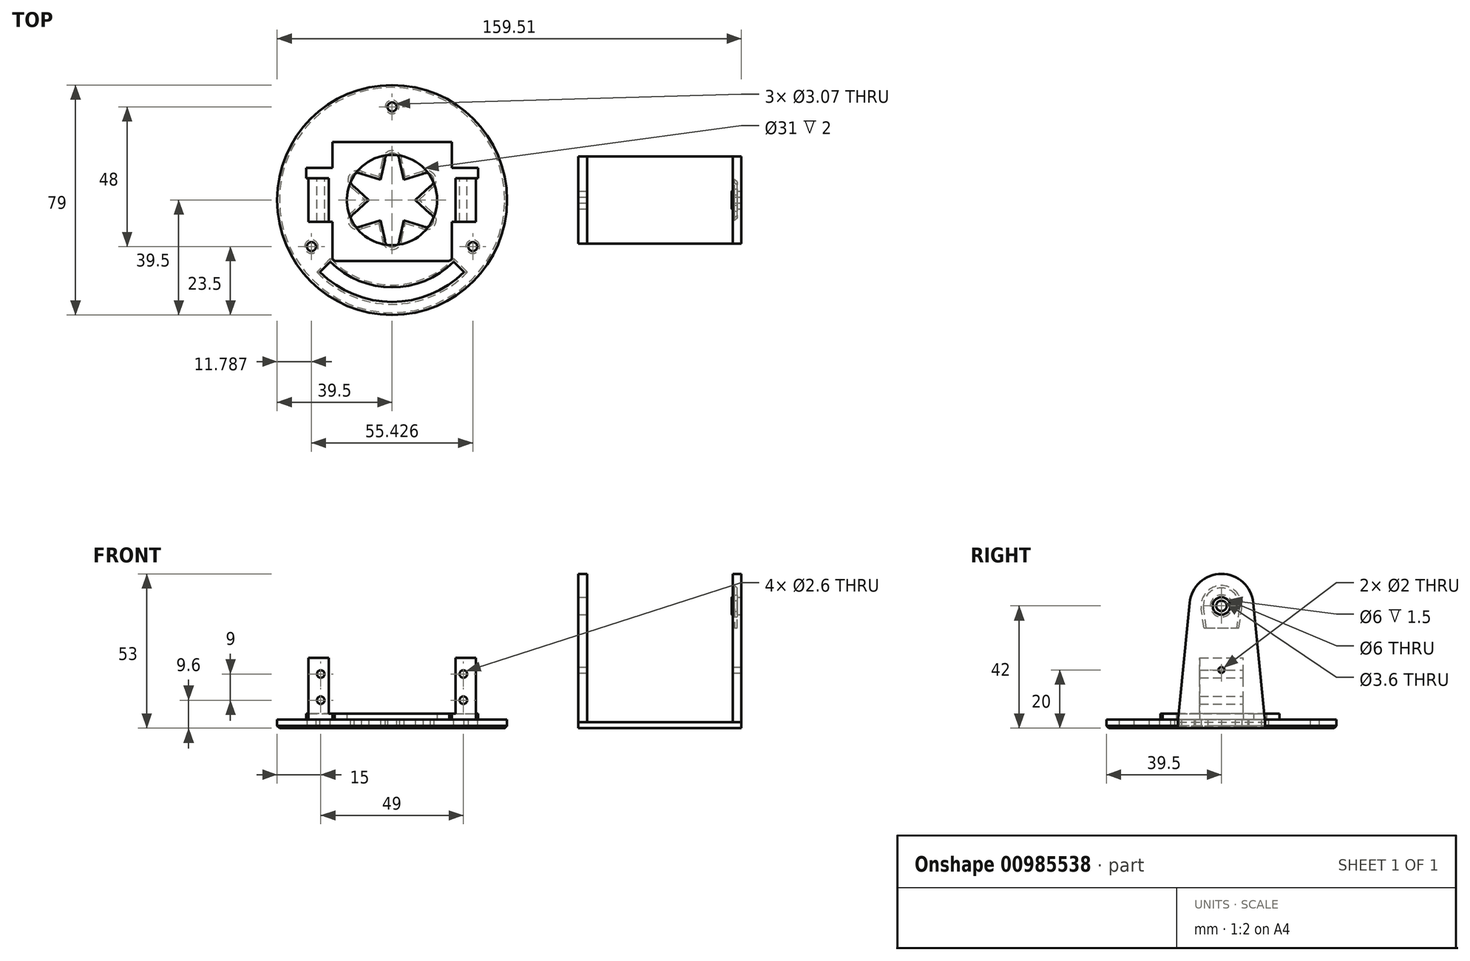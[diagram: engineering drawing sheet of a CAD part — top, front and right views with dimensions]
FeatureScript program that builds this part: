
annotation { "Feature Type Name" : "Feature", "Feature Type Description" : "" }
export const myFeature = defineFeature(function(context is Context, id is Id, definition is map)
    precondition{}
    {
        {
            var Q0;
            Q0=qCreatedBy(makeId("Top.planeOp"),FACE);
            var sketch = newSketch(context, id + "F0", { "sketchPlane" : qUnion([Q0])});
            skCircle(sketch, "E0", {"center": v(0, 0) * mm, "radius": 39.5 * mm});
            skLineSegment(sketch, "E1", {"start": v(0, 6.93) * mm, "end": v(0, 13.68) * mm});
            skArc(sketch, "E2", {"start": v(2.5, 13.68) * mm, "mid": v(0, 16.18) * mm, "end": v(-2.5, 13.68) * mm});
            skLineSegment(sketch, "E3", {"start": v(2.5, 13.68) * mm, "end": v(4, 6.93) * mm});
            skLineSegment(sketch, "E4", {"start": v(-2.5, 13.68) * mm, "end": v(-4, 6.93) * mm});
            skLineSegment(sketch, "E5", {"start": v(0, 0) * mm, "end": v(0, 6.93) * mm});
            skLineSegment(sketch, "E6", {"start": v(-4, 6.93) * mm, "end": v(0, 0) * mm});
            skLineSegment(sketch, "E7", {"start": v(4, 6.93) * mm, "end": v(0, 0) * mm});
            skLineSegment(sketch, "E8.1.0", {"start": v(-10.6, 9) * mm, "end": v(-4, 6.93) * mm});
            skLineSegment(sketch, "E8.1.1", {"start": v(-8, 0) * mm, "end": v(0, 0) * mm});
            skLineSegment(sketch, "E8.1.2", {"start": v(-6, 3.46) * mm, "end": v(-11.85, 6.84) * mm});
            skLineSegment(sketch, "E8.1.3", {"start": v(0, 0) * mm, "end": v(-6, 3.46) * mm});
            skArc(sketch, "E8.1.4", {"start": v(-10.6, 9) * mm, "mid": v(-14.01, 8.09) * mm, "end": v(-13.1, 4.67) * mm});
            skLineSegment(sketch, "E8.1.5", {"start": v(-13.1, 4.67) * mm, "end": v(-8, 0) * mm});
            skLineSegment(sketch, "E8.2.0", {"start": v(-13.1, -4.67) * mm, "end": v(-8, 0) * mm});
            skLineSegment(sketch, "E8.2.1", {"start": v(-4, -6.93) * mm, "end": v(0, 0) * mm});
            skLineSegment(sketch, "E8.2.2", {"start": v(-6, -3.46) * mm, "end": v(-11.85, -6.84) * mm});
            skLineSegment(sketch, "E8.2.3", {"start": v(0, 0) * mm, "end": v(-6, -3.46) * mm});
            skArc(sketch, "E8.2.4", {"start": v(-13.1, -4.67) * mm, "mid": v(-14.01, -8.09) * mm, "end": v(-10.6, -9) * mm});
            skLineSegment(sketch, "E8.2.5", {"start": v(-10.6, -9) * mm, "end": v(-4, -6.93) * mm});
            skLineSegment(sketch, "E8.2.6", {"start": v(-8, 0) * mm, "end": v(0, 0) * mm});
            skLineSegment(sketch, "E8.3.0", {"start": v(-2.5, -13.68) * mm, "end": v(-4, -6.93) * mm});
            skLineSegment(sketch, "E8.3.1", {"start": v(4, -6.93) * mm, "end": v(0, 0) * mm});
            skLineSegment(sketch, "E8.3.2", {"start": v(0, -6.93) * mm, "end": v(0, -13.68) * mm});
            skLineSegment(sketch, "E8.3.3", {"start": v(0, 0) * mm, "end": v(0, -6.93) * mm});
            skArc(sketch, "E8.3.4", {"start": v(-2.5, -13.68) * mm, "mid": v(0, -16.18) * mm, "end": v(2.5, -13.68) * mm});
            skLineSegment(sketch, "E8.3.5", {"start": v(2.5, -13.68) * mm, "end": v(4, -6.93) * mm});
            skLineSegment(sketch, "E8.3.6", {"start": v(-4, -6.93) * mm, "end": v(0, 0) * mm});
            skLineSegment(sketch, "E8.4.0", {"start": v(10.6, -9) * mm, "end": v(4, -6.93) * mm});
            skLineSegment(sketch, "E8.4.1", {"start": v(8, 0) * mm, "end": v(0, 0) * mm});
            skLineSegment(sketch, "E8.4.2", {"start": v(6, -3.46) * mm, "end": v(11.85, -6.84) * mm});
            skLineSegment(sketch, "E8.4.3", {"start": v(0, 0) * mm, "end": v(6, -3.46) * mm});
            skArc(sketch, "E8.4.4", {"start": v(10.6, -9) * mm, "mid": v(14.01, -8.09) * mm, "end": v(13.1, -4.67) * mm});
            skLineSegment(sketch, "E8.4.5", {"start": v(13.1, -4.67) * mm, "end": v(8, 0) * mm});
            skLineSegment(sketch, "E8.4.6", {"start": v(4, -6.93) * mm, "end": v(0, 0) * mm});
            skLineSegment(sketch, "E8.5.0", {"start": v(13.1, 4.67) * mm, "end": v(8, 0) * mm});
            skLineSegment(sketch, "E8.5.2", {"start": v(6, 3.46) * mm, "end": v(11.85, 6.84) * mm});
            skLineSegment(sketch, "E8.5.3", {"start": v(0, 0) * mm, "end": v(6, 3.46) * mm});
            skArc(sketch, "E8.5.4", {"start": v(13.1, 4.67) * mm, "mid": v(14.01, 8.09) * mm, "end": v(10.6, 9) * mm});
            skLineSegment(sketch, "E8.5.5", {"start": v(10.6, 9) * mm, "end": v(4, 6.93) * mm});
            skLineSegment(sketch, "E8.5.6", {"start": v(8, 0) * mm, "end": v(0, 0) * mm});
            skCircle(sketch, "E9", {"center": v(0, 32) * mm, "radius": 1.53 * mm});
            skCircle(sketch, "E10.1.0", {"center": v(-27.71, -16) * mm, "radius": 1.53 * mm});
            skCircle(sketch, "E10.2.0", {"center": v(27.71, -16) * mm, "radius": 1.53 * mm});
            skSolve(sketch);
        }
        {
            var Q0;
            Q0=qSketchRegion(id+"F0",true);
            extrude(context, id + "F1", {"entities" : qUnion([Q0]), "depth" : 3 * mm, "offsetDistance" : 25 * mm});
        }
        {
            var Q0;
            Q0=makeQuery(id+"F1.opExtrude","CAP_FACE",FACE,{"disambiguationData":[OSD([sQuery(id+"F0.wireOp",EDGE,"E0"),sQuery(id+"F0.wireOp",EDGE,"tsmetPdh-uBPC-VMs7-KmTe-eYArdxmcJazE.bottom"),sQuery(id+"F0.wireOp",EDGE,"tsmetPdh-uBPC-VMs7-KmTe-eYArdxmcJazE.top"),sQuery(id+"F0.wireOp",EDGE,"tsmetPdh-uBPC-VMs7-KmTe-eYArdxmcJazE.left"),sQuery(id+"F0.wireOp",EDGE,"tsmetPdh-uBPC-VMs7-KmTe-eYArdxmcJazE.right"),sQuery(id+"F0.wireOp",EDGE,"4L8ITVok-LRZH-0QI6-TBfI-3UofOHPGhmV9.bottom"),sQuery(id+"F0.wireOp",EDGE,"4L8ITVok-LRZH-0QI6-TBfI-3UofOHPGhmV9.top"),sQuery(id+"F0.wireOp",EDGE,"4L8ITVok-LRZH-0QI6-TBfI-3UofOHPGhmV9.right"),sQuery(id+"F0.wireOp",EDGE,"eeb0b982-9b75-4dce-bc6a-ac392abf8ab80.MirrorCS"),sQuery(id+"F0.wireOp",EDGE,"f73e68d2-0441-471e-96cc-38fd0b7eeaf80.MirrorCS"),sQuery(id+"F0.wireOp",EDGE,"16b79043-1bf6-4525-a8b7-725060b6b32b0.MirrorCS"),sQuery(id+"F0.wireOp",EDGE,"p6ZJKreq-HdhA-XT4y-qAaR-6FUMRbpX3NII"),sQuery(id+"F0.wireOp",EDGE,"b497d003-922a-44de-87ad-1ec905d6c705.1.0"),sQuery(id+"F0.wireOp",EDGE,"b497d003-922a-44de-87ad-1ec905d6c705.2.0"),sQuery(id+"F0.wireOp",EDGE,"b497d003-922a-44de-87ad-1ec905d6c705.3.0"),sQuery(id+"F0.wireOp",EDGE,"b497d003-922a-44de-87ad-1ec905d6c705.4.0"),sQuery(id+"F0.wireOp",EDGE,"b497d003-922a-44de-87ad-1ec905d6c705.5.0")])],"isStart":false});
            var sketch = newSketch(context, id + "F2", { "sketchPlane" : qUnion([Q0])});
            skLineSegment(sketch, "E11.bottom", {"start": v(20.5, -21) * mm, "end": v(-20.5, -21) * mm});
            skLineSegment(sketch, "E11.top", {"start": v(20.5, 20) * mm, "end": v(-20.5, 20) * mm});
            skLineSegment(sketch, "E11.left", {"start": v(20.5, -21) * mm, "end": v(20.5, 20) * mm});
            skLineSegment(sketch, "E11.right", {"start": v(-20.5, -21) * mm, "end": v(-20.5, 20) * mm});
            skPoint(sketch, "E11.middle", {"position": v(0, -0.5) * mm});
            skPoint(sketch, "E12", {"position": v(0, -3.9) * mm});
            skLineSegment(sketch, "E13.bottom", {"start": v(20.5, 11) * mm, "end": v(29.5, 11) * mm});
            skLineSegment(sketch, "E13.top", {"start": v(20.5, 7.5) * mm, "end": v(29.5, 7.5) * mm});
            skLineSegment(sketch, "E13.left", {"start": v(20.5, 11) * mm, "end": v(20.5, 7.5) * mm});
            skLineSegment(sketch, "E13.right", {"start": v(29.5, 11) * mm, "end": v(29.5, 7.5) * mm});
            skPoint(sketch, "E14.center", {"position": v(0, 0) * mm});
            skLineSegment(sketch, "E15", {"start": v(28.75, 7.5) * mm, "end": v(28.75, -7.5) * mm});
            skLineSegment(sketch, "E16", {"start": v(28.75, -7.5) * mm, "end": v(19.95, -7.5) * mm});
            skLineSegment(sketch, "E17.MirrorCS", {"start": v(-20.5, 11) * mm, "end": v(-29.5, 11) * mm});
            skLineSegment(sketch, "E18.MirrorCS", {"start": v(-29.5, 11) * mm, "end": v(-29.5, 7.5) * mm});
            skLineSegment(sketch, "E19.MirrorCS", {"start": v(-20.5, 7.5) * mm, "end": v(-29.5, 7.5) * mm});
            skLineSegment(sketch, "E20.MirrorCS", {"start": v(-28.75, 7.5) * mm, "end": v(-28.75, -7.5) * mm});
            skLineSegment(sketch, "E21.MirrorCS", {"start": v(-28.75, -7.5) * mm, "end": v(-19.95, -7.5) * mm});
            skCircle(sketch, "E22", {"center": v(0, 0) * mm, "radius": 15.5 * mm});
            skSolve(sketch);
        }
        {
            var Q0;
            {var subQ6=sQuery(id+"F2.wireOp",EDGE,"E15");var subQ9=sQuery(id+"F2.wireOp",EDGE,"E17.MirrorCS");var subQ15=sQuery(id+"F2.wireOp",EDGE,"E22");var subQ16=makeQuery(id+"F1.opExtrude","CAP_EDGE",EDGE,{"disambiguationData":[OSD([sQuery(id+"F0.wireOp",EDGE,"E8.1.4")])],"isStart":false});var subQ17=makeQuery(id+"F2.imprint","INTERSECT",VERTEX,{"disambiguationData":[OD(0.0)],"derivedFrom":[subQ16,subQ15]});var subQ21=makeQuery(id+"F1.opExtrude","CAP_EDGE",EDGE,{"disambiguationData":[OSD([sQuery(id+"F0.wireOp",EDGE,"E8.3.4")])],"isStart":false});var subQ23=makeQuery(id+"F1.opExtrude","CAP_EDGE",EDGE,{"disambiguationData":[OSD([sQuery(id+"F0.wireOp",EDGE,"E8.4.4")])],"isStart":false});var subQ24=makeQuery(id+"F2.imprint","INTERSECT",VERTEX,{"disambiguationData":[OD(0.0)],"derivedFrom":[subQ23,subQ15]});var subQ25=sQuery(id+"F2.wireOp",EDGE,"E11.bottom");var subQ29=makeQuery(id+"F1.opExtrude","CAP_EDGE",EDGE,{"disambiguationData":[OSD([sQuery(id+"F0.wireOp",EDGE,"E8.2.4")])],"isStart":false});var subQ31=makeQuery(id+"F2.imprint","INTERSECT",VERTEX,{"disambiguationData":[OD(0.0)],"derivedFrom":[subQ21,subQ15]});var subQ32=makeQuery(id+"F1.opExtrude","CAP_EDGE",EDGE,{"disambiguationData":[OSD([sQuery(id+"F0.wireOp",EDGE,"E2")])],"isStart":false});var subQ33=makeQuery(id+"F2.imprint","INTERSECT",VERTEX,{"disambiguationData":[OD(0.0)],"derivedFrom":[subQ32,subQ15]});var subQ36=sQuery(id+"F2.wireOp",EDGE,"E13.bottom");var subQ39=makeQuery(id+"F2.imprint","INTERSECT",VERTEX,{"disambiguationData":[OD(0.0)],"derivedFrom":[subQ29,subQ15]});var subQ40=makeQuery(id+"F1.opExtrude","CAP_EDGE",EDGE,{"disambiguationData":[OSD([sQuery(id+"F0.wireOp",EDGE,"E8.5.4")])],"isStart":false});var subQ41=makeQuery(id+"F2.imprint","INTERSECT",VERTEX,{"disambiguationData":[OD(0.0)],"derivedFrom":[subQ40,subQ15]});var subQ48=sQuery(id+"F2.wireOp",EDGE,"E20.MirrorCS");Q0=qUnion([makeQuery(id+"F2.imprint","IMPRINT",FACE,{"disambiguationData":[TD([[makeQuery(id+"F2.imprint","IMPRINT",EDGE,{"derivedFrom":subQ9}),1.0]])]}),makeQuery(id+"F2.imprint","IMPRINT",FACE,{"disambiguationData":[TD([[makeQuery(id+"F2.imprint","IMPRINT",EDGE,{"disambiguationData":[TD([[subQ17,-1.0]])],"derivedFrom":subQ15}),-1.0]])]}),makeQuery(id+"F2.imprint","IMPRINT",FACE,{"disambiguationData":[TD([[makeQuery(id+"F2.imprint","IMPRINT",EDGE,{"derivedFrom":subQ36}),-1.0]])]}),makeQuery(id+"F2.imprint","IMPRINT",FACE,{"disambiguationData":[TD([[makeQuery(id+"F2.imprint","IMPRINT",EDGE,{"disambiguationData":[TD([[subQ24,-1.0]])],"derivedFrom":subQ15}),-1.0]])]}),makeQuery(id+"F2.imprint","IMPRINT",FACE,{"disambiguationData":[TD([[makeQuery(id+"F2.imprint","IMPRINT",EDGE,{"disambiguationData":[TD([[subQ39,-1.0]])],"derivedFrom":subQ15}),-1.0]])]}),makeQuery(id+"F2.imprint","IMPRINT",FACE,{"disambiguationData":[TD([[makeQuery(id+"F2.imprint","IMPRINT",EDGE,{"derivedFrom":subQ48}),1.0]])]}),makeQuery(id+"F2.imprint","IMPRINT",FACE,{"disambiguationData":[TD([[makeQuery(id+"F2.imprint","IMPRINT",EDGE,{"disambiguationData":[TD([[subQ41,1.0]])],"derivedFrom":subQ15}),-1.0]])]}),makeQuery(id+"F2.imprint","IMPRINT",FACE,{"disambiguationData":[TD([[makeQuery(id+"F2.imprint","IMPRINT",EDGE,{"disambiguationData":[TD([[subQ31,-1.0]])],"derivedFrom":subQ15}),-1.0]])]}),makeQuery(id+"F2.imprint","IMPRINT",FACE,{"disambiguationData":[TD([[makeQuery(id+"F2.imprint","IMPRINT",EDGE,{"disambiguationData":[TD([[subQ33,-1.0]])],"derivedFrom":subQ15}),-1.0]])]}),makeQuery(id+"F2.imprint","IMPRINT",FACE,{"disambiguationData":[TD([[makeQuery(id+"F2.imprint","IMPRINT",EDGE,{"derivedFrom":subQ25}),-1.0]])]}),makeQuery(id+"F2.imprint","IMPRINT",FACE,{"disambiguationData":[TD([[makeQuery(id+"F2.imprint","IMPRINT",EDGE,{"derivedFrom":subQ6}),-1.0]])]})]);}
            extrude(context, id + "F3", {"entities" : qUnion([Q0]), "operationType" : NewBodyOperationType.ADD, "depth" : 2 * mm, "offsetDistance" : 25 * mm});
        }
        {
            var Q0;
            Q0=qCreatedBy(makeId("Front.planeOp"),FACE);
            var sketch = newSketch(context, id + "F4", { "sketchPlane" : qUnion([Q0])});
            skLineSegment(sketch, "E23", {"start": v(9.75, 14.1) * mm, "end": v(14.35, 14.1) * mm});
            skCircle(sketch, "E24", {"center": v(24.5, 18.6) * mm, "radius": 1.3 * mm});
            skLineSegment(sketch, "E25.bottom", {"start": v(21.75, 4) * mm, "end": v(21.75, 24.2) * mm});
            skLineSegment(sketch, "E25.top", {"start": v(28.75, 4) * mm, "end": v(28.75, 24.2) * mm});
            skLineSegment(sketch, "E25.left", {"start": v(21.75, 4) * mm, "end": v(28.75, 4) * mm});
            skLineSegment(sketch, "E25.right", {"start": v(21.75, 24.2) * mm, "end": v(28.75, 24.2) * mm});
            skPoint(sketch, "E25.middle", {"position": v(25.25, 14.1) * mm});
            skCircle(sketch, "E26.MirrorC", {"center": v(24.5, 9.6) * mm, "radius": 1.3 * mm});
            skLineSegment(sketch, "E27", {"start": v(0, 7.04) * mm, "end": v(0, 23.64) * mm});
            skPoint(sketch, "E28.MirrorP", {"position": v(-25.25, 14.1) * mm});
            skLineSegment(sketch, "E29.MirrorCS", {"start": v(-21.75, 24.2) * mm, "end": v(-28.75, 24.2) * mm});
            skLineSegment(sketch, "E30.MirrorCS", {"start": v(-28.75, 4) * mm, "end": v(-28.75, 24.2) * mm});
            skLineSegment(sketch, "E31.MirrorCS", {"start": v(-21.75, 4) * mm, "end": v(-21.75, 24.2) * mm});
            skCircle(sketch, "E32.MirrorC", {"center": v(-24.5, 9.6) * mm, "radius": 1.3 * mm});
            skLineSegment(sketch, "E33.MirrorCS", {"start": v(-21.75, 4) * mm, "end": v(-28.75, 4) * mm});
            skCircle(sketch, "E34.MirrorC", {"center": v(-24.5, 18.6) * mm, "radius": 1.3 * mm});
            skSolve(sketch);
        }
        {
            var Q0;
            Q0 = qSketchRegion(id + "F4", true);
            extrude(context, id + "F5", {"entities" : qUnion([Q0]), "operationType" : NewBodyOperationType.ADD, "endBound" : BoundingType.SYMMETRIC, "depth" : 15 * mm, "offsetDistance" : 25 * mm});
        }
        {
            var Q0;
            Q0=qCreatedBy(makeId("Top.planeOp"),FACE);
            var sketch = newSketch(context, id + "F6", { "sketchPlane" : qUnion([Q0])});
            skLineSegment(sketch, "E35.bottom", {"start": v(120.01, -15) * mm, "end": v(64.01, -15) * mm});
            skLineSegment(sketch, "E35.top", {"start": v(120.01, 15) * mm, "end": v(64.01, 15) * mm});
            skLineSegment(sketch, "E35.left", {"start": v(120.01, -15) * mm, "end": v(120.01, 15) * mm});
            skLineSegment(sketch, "E35.right", {"start": v(64.01, -15) * mm, "end": v(64.01, 15) * mm});
            skPoint(sketch, "E35.middle", {"position": v(92.01, 0) * mm});
            skSolve(sketch);
        }
        {
            var Q0;
            Q0=makeQuery(id+"F6.imprint","IMPRINT",FACE,{"disambiguationData":[TD([[makeQuery(id+"F6.imprint","IMPRINT",EDGE,{"derivedFrom":sQuery(id+"F6.wireOp",EDGE,"E35.bottom")}),-1.0]])]});
            extrude(context, id + "F7", {"entities" : qUnion([Q0]), "depth" : 2 * mm, "offsetDistance" : 25 * mm});
        }
        {
            var Q0;
            Q0=makeQuery(id+"F7.opExtrude","SWEPT_FACE",FACE,{"disambiguationData":[OSD([sQuery(id+"F6.wireOp",EDGE,"E35.left")])]});
            var sketch = newSketch(context, id + "F8", { "sketchPlane" : qUnion([Q0])});
            skCircle(sketch, "E36", {"center": v(0, 42) * mm, "radius": 11 * mm});
            skLineSegment(sketch, "E37", {"start": v(0, 2) * mm, "end": v(15, 2) * mm});
            skLineSegment(sketch, "E38", {"start": v(15, 2) * mm, "end": v(10.95, 43.08) * mm});
            skLineSegment(sketch, "E39.MirrorCS", {"start": v(-15, 2) * mm, "end": v(-10.95, 43.08) * mm});
            skLineSegment(sketch, "E40.MirrorCS", {"start": v(0, 2) * mm, "end": v(-15, 2) * mm});
            skCircle(sketch, "E41", {"center": v(0, 20) * mm, "radius": 1 * mm});
            skCircle(sketch, "E42", {"center": v(0, 42) * mm, "radius": 3 * mm});
            skSolve(sketch);
        }
        {
            var Q0;
            Q0=qSketchRegion(id+"F8",true);
            extrude(context, id + "F9", {"entities" : qUnion([Q0]), "oppositeDirection" : true, "depth" : 3 * mm, "offsetDistance" : 25 * mm});
        }
        {
            var Q0;
            Q0=makeQuery(id+"F9.opExtrude","SWEPT_BODY",BODY,{"disambiguationData":[OSD([sQuery(id+"F8.wireOp",EDGE,"E36"),sQuery(id+"F8.wireOp",EDGE,"E37"),sQuery(id+"F8.wireOp",EDGE,"E38"),sQuery(id+"F8.wireOp",EDGE,"E39.MirrorCS"),sQuery(id+"F8.wireOp",EDGE,"E40.MirrorCS")])]});
            transform(context, id + "F10", {"entities" : qUnion([Q0]), "transformType" : TransformType.TRANSLATION_3D, "dx" : -53 * mm, "dy" : 0 * mm, "dz" : 0 * mm, "makeCopy" : true});
        }
        {
            var Q0;
            Q0=makeQuery(id+"F7.opExtrude","SWEPT_BODY",BODY,{"disambiguationData":[OSD([sQuery(id+"F6.wireOp",EDGE,"E35.bottom"),sQuery(id+"F6.wireOp",EDGE,"E35.top"),sQuery(id+"F6.wireOp",EDGE,"E35.left"),sQuery(id+"F6.wireOp",EDGE,"E35.right")])]});
            var Q1;
            Q1=makeQuery(id+"F9.opExtrude","SWEPT_BODY",BODY,{"disambiguationData":[OSD([sQuery(id+"F8.wireOp",EDGE,"E36"),sQuery(id+"F8.wireOp",EDGE,"E37"),sQuery(id+"F8.wireOp",EDGE,"E38"),sQuery(id+"F8.wireOp",EDGE,"E39.MirrorCS"),sQuery(id+"F8.wireOp",EDGE,"E40.MirrorCS")])]});
            var Q2;
            Q2=makeQuery(id+"F10.opPattern","COPY",BODY,{"derivedFrom":makeQuery(id+"F9.opExtrude","SWEPT_BODY",BODY,{"disambiguationData":[OSD([sQuery(id+"F8.wireOp",EDGE,"E36"),sQuery(id+"F8.wireOp",EDGE,"E37"),sQuery(id+"F8.wireOp",EDGE,"E38"),sQuery(id+"F8.wireOp",EDGE,"E39.MirrorCS"),sQuery(id+"F8.wireOp",EDGE,"E40.MirrorCS"),sQuery(id+"F8.wireOp",EDGE,"E41"),sQuery(id+"F8.wireOp",EDGE,"E42")])]}),"instanceName":"1"});
            booleanBodies(context, id + "F11", {"operationType" : BooleanOperationType.UNION, "tools" : qUnion([Q0, Q1, Q2])});
        }
        {
            var Q0;
            Q0=makeQuery(id+"F9.opExtrude","CAP_FACE",FACE,{"disambiguationData":[OSD([sQuery(id+"F8.wireOp",EDGE,"E36"),sQuery(id+"F8.wireOp",EDGE,"E37"),sQuery(id+"F8.wireOp",EDGE,"E38"),sQuery(id+"F8.wireOp",EDGE,"E39.MirrorCS"),sQuery(id+"F8.wireOp",EDGE,"E40.MirrorCS")])],"isStart":false});
            var sketch = newSketch(context, id + "F12", { "sketchPlane" : qUnion([Q0])});
            skCircle(sketch, "E43", {"center": v(0, 42) * mm, "radius": 7 * mm});
            skLineSegment(sketch, "E44", {"start": v(6, 34.4) * mm, "end": v(-6, 34.4) * mm});
            skLineSegment(sketch, "E45", {"start": v(0, 31.56) * mm, "end": v(0, 34.4) * mm});
            skLineSegment(sketch, "E46", {"start": v(-6, 34.4) * mm, "end": v(-6.93, 41.03) * mm});
            skLineSegment(sketch, "E47.MirrorCS", {"start": v(6, 34.4) * mm, "end": v(6.93, 41.03) * mm});
            skSolve(sketch);
        }
        {
            var Q0;
            Q0=qSketchRegion(id+"F12",true);
            extrude(context, id + "F13", {"entities" : qUnion([Q0]), "operationType" : NewBodyOperationType.REMOVE, "oppositeDirection" : true, "depth" : 1.5 * mm, "offsetDistance" : 25 * mm});
        }
        {
            var Q0;
            Q0=makeQuery(id+"F13.boolean.opBoolean","COPY",FACE,{"derivedFrom":makeQuery(id+"F13.opExtrude","CAP_FACE",FACE,{"disambiguationData":[OSD([sQuery(id+"F12.wireOp",EDGE,"E43"),sQuery(id+"F12.wireOp",EDGE,"E44"),sQuery(id+"F12.wireOp",EDGE,"E46"),sQuery(id+"F12.wireOp",EDGE,"E47.MirrorCS")])],"isStart":false})});
            var sketch = newSketch(context, id + "F14", { "sketchPlane" : qUnion([Q0])});
            skCircle(sketch, "E48", {"center": v(0, 42) * mm, "radius": 3.8 * mm});
            skCircle(sketch, "E49", {"center": v(0, 42) * mm, "radius": 1.8 * mm});
            skSolve(sketch);
        }
        {
            var Q0;
            Q0=qSketchRegion(id+"F14",true);
            extrude(context, id + "F15", {"entities" : qUnion([Q0]), "operationType" : NewBodyOperationType.ADD, "depth" : 1.8 * mm, "offsetDistance" : 25 * mm});
        }
        {
            var Q0;
            Q0=makeQuery(id+"F13.boolean.opBoolean","COPY",EDGE,{"derivedFrom":makeQuery(id+"F13.opExtrude","CAP_EDGE",EDGE,{"disambiguationData":[OSD([sQuery(id+"F12.wireOp",EDGE,"E43")])],"isStart":false})});
            var Q1;
            Q1=makeQuery(id+"F15.opExtrude","CAP_EDGE",EDGE,{"disambiguationData":[OSD([sQuery(id+"F14.wireOp",EDGE,"E48")])],"isStart":false});
            chamfer(context, id + "F16", {"entities" : qUnion([Q0, Q1]), "width" : .8 * mm, "tangentPropagation" : true});
        }
        {
            var Q0;
            {var subQ8=sQuery(id+"F0.wireOp",EDGE,"E9");var subQ9=sQuery(id+"F0.wireOp",EDGE,"E0");var subQ10=sQuery(id+"F0.wireOp",EDGE,"E10.2.0");var subQ11=sQuery(id+"F0.wireOp",EDGE,"E10.1.0");Q0=makeQuery(id+"F3.boolean.opBoolean","SPLIT",FACE,{"disambiguationData":[TD([makeQuery(id+"F1.opExtrude","SWEPT_FACE",FACE,{"disambiguationData":[OSD([subQ9])]})])],"derivedFrom":makeQuery(id+"F1.opExtrude","CAP_FACE",FACE,{"disambiguationData":[OSD([subQ9,sQuery(id+"F0.wireOp",EDGE,"E2"),sQuery(id+"F0.wireOp",EDGE,"E3"),sQuery(id+"F0.wireOp",EDGE,"E4"),sQuery(id+"F0.wireOp",EDGE,"E8.1.0"),sQuery(id+"F0.wireOp",EDGE,"E8.1.4"),sQuery(id+"F0.wireOp",EDGE,"E8.1.5"),sQuery(id+"F0.wireOp",EDGE,"E8.2.0"),sQuery(id+"F0.wireOp",EDGE,"E8.2.4"),sQuery(id+"F0.wireOp",EDGE,"E8.2.5"),sQuery(id+"F0.wireOp",EDGE,"E8.3.0"),sQuery(id+"F0.wireOp",EDGE,"E8.3.4"),sQuery(id+"F0.wireOp",EDGE,"E8.3.5"),sQuery(id+"F0.wireOp",EDGE,"E8.4.0"),sQuery(id+"F0.wireOp",EDGE,"E8.4.4"),sQuery(id+"F0.wireOp",EDGE,"E8.4.5"),sQuery(id+"F0.wireOp",EDGE,"E8.5.0"),sQuery(id+"F0.wireOp",EDGE,"E8.5.4"),sQuery(id+"F0.wireOp",EDGE,"E8.5.5"),subQ8,subQ11,subQ10])],"isStart":false})});}
            var sketch = newSketch(context, id + "F17", { "sketchPlane" : qUnion([Q0])});
            skArc(sketch, "E50", {"start": v(-24.75, -24.75) * mm, "mid": v(0, -35) * mm, "end": v(24.75, -24.75) * mm});
            skArc(sketch, "E51", {"start": v(-21.21, -21.21) * mm, "mid": v(0, -30) * mm, "end": v(21.21, -21.21) * mm});
            skLineSegment(sketch, "E52", {"start": v(21.21, -21.21) * mm, "end": v(24.75, -24.75) * mm});
            skLineSegment(sketch, "E53.MirrorCS", {"start": v(-21.21, -21.21) * mm, "end": v(-24.75, -24.75) * mm});
            skSolve(sketch);
        }
        {
            var Q0;
            Q0 = qSketchRegion(id + "F17", true);
            extrude(context, id + "F18", {"entities" : qUnion([Q0]), "operationType" : NewBodyOperationType.REMOVE, "oppositeDirection" : true, "depth" : 25 * mm, "offsetDistance" : 25 * mm});
        }
        {
            var Q0;
            Q0=makeQuery(id+"F3.opExtrude","SWEPT_EDGE",EDGE,{"disambiguationData":[OSD([sQuery(id+"F2.wireOp",EDGE,"E11.bottom"),sQuery(id+"F2.wireOp",EDGE,"E11.right")])]});
            var Q1;
            Q1=makeQuery(id+"F3.opExtrude","SWEPT_EDGE",EDGE,{"disambiguationData":[OSD([sQuery(id+"F2.wireOp",EDGE,"E11.bottom"),sQuery(id+"F2.wireOp",EDGE,"E11.left")])]});
            var Q2;
            Q2=makeQuery(id+"F18.boolean.opBoolean","COPY",EDGE,{"derivedFrom":makeQuery(id+"F18.opExtrude","CAP_EDGE",EDGE,{"disambiguationData":[OSD([sQuery(id+"F17.wireOp",EDGE,"E51")])],"isStart":true})});
            var Q3;
            Q3=makeQuery(id+"F18.boolean.opBoolean","COPY",EDGE,{"derivedFrom":makeQuery(id+"F18.opExtrude","CAP_EDGE",EDGE,{"disambiguationData":[OSD([sQuery(id+"F17.wireOp",EDGE,"E53.MirrorCS")])],"isStart":true})});
            var Q4;
            Q4=makeQuery(id+"F18.boolean.opBoolean","COPY",EDGE,{"derivedFrom":makeQuery(id+"F18.opExtrude","CAP_EDGE",EDGE,{"disambiguationData":[OSD([sQuery(id+"F17.wireOp",EDGE,"E50")])],"isStart":true})});
            var Q5;
            Q5=makeQuery(id+"F18.boolean.opBoolean","COPY",EDGE,{"derivedFrom":makeQuery(id+"F18.opExtrude","CAP_EDGE",EDGE,{"disambiguationData":[OSD([sQuery(id+"F17.wireOp",EDGE,"E52")])],"isStart":true})});
            var Q6;
            Q6=makeQuery(id+"F18.boolean.opBoolean","INTERSECT",EDGE,{"derivedFrom":[makeQuery(id+"F1.opExtrude","CAP_FACE",FACE,{"disambiguationData":[OSD([sQuery(id+"F0.wireOp",EDGE,"E0"),sQuery(id+"F0.wireOp",EDGE,"E2"),sQuery(id+"F0.wireOp",EDGE,"E3"),sQuery(id+"F0.wireOp",EDGE,"E4"),sQuery(id+"F0.wireOp",EDGE,"E8.1.0"),sQuery(id+"F0.wireOp",EDGE,"E8.1.4"),sQuery(id+"F0.wireOp",EDGE,"E8.1.5"),sQuery(id+"F0.wireOp",EDGE,"E8.2.0"),sQuery(id+"F0.wireOp",EDGE,"E8.2.4"),sQuery(id+"F0.wireOp",EDGE,"E8.2.5"),sQuery(id+"F0.wireOp",EDGE,"E8.3.0"),sQuery(id+"F0.wireOp",EDGE,"E8.3.4"),sQuery(id+"F0.wireOp",EDGE,"E8.3.5"),sQuery(id+"F0.wireOp",EDGE,"E8.4.0"),sQuery(id+"F0.wireOp",EDGE,"E8.4.4"),sQuery(id+"F0.wireOp",EDGE,"E8.4.5"),sQuery(id+"F0.wireOp",EDGE,"E8.5.0"),sQuery(id+"F0.wireOp",EDGE,"E8.5.4"),sQuery(id+"F0.wireOp",EDGE,"E8.5.5"),sQuery(id+"F0.wireOp",EDGE,"E9"),sQuery(id+"F0.wireOp",EDGE,"E10.1.0"),sQuery(id+"F0.wireOp",EDGE,"E10.2.0")])],"isStart":true}),makeQuery(id+"F18.opExtrude","SWEPT_FACE",FACE,{"disambiguationData":[OSD([sQuery(id+"F17.wireOp",EDGE,"E51")])]})]});
            var Q7;
            Q7=makeQuery(id+"F18.boolean.opBoolean","INTERSECT",EDGE,{"derivedFrom":[makeQuery(id+"F1.opExtrude","CAP_FACE",FACE,{"disambiguationData":[OSD([sQuery(id+"F0.wireOp",EDGE,"E0"),sQuery(id+"F0.wireOp",EDGE,"E2"),sQuery(id+"F0.wireOp",EDGE,"E3"),sQuery(id+"F0.wireOp",EDGE,"E4"),sQuery(id+"F0.wireOp",EDGE,"E8.1.0"),sQuery(id+"F0.wireOp",EDGE,"E8.1.4"),sQuery(id+"F0.wireOp",EDGE,"E8.1.5"),sQuery(id+"F0.wireOp",EDGE,"E8.2.0"),sQuery(id+"F0.wireOp",EDGE,"E8.2.4"),sQuery(id+"F0.wireOp",EDGE,"E8.2.5"),sQuery(id+"F0.wireOp",EDGE,"E8.3.0"),sQuery(id+"F0.wireOp",EDGE,"E8.3.4"),sQuery(id+"F0.wireOp",EDGE,"E8.3.5"),sQuery(id+"F0.wireOp",EDGE,"E8.4.0"),sQuery(id+"F0.wireOp",EDGE,"E8.4.4"),sQuery(id+"F0.wireOp",EDGE,"E8.4.5"),sQuery(id+"F0.wireOp",EDGE,"E8.5.0"),sQuery(id+"F0.wireOp",EDGE,"E8.5.4"),sQuery(id+"F0.wireOp",EDGE,"E8.5.5"),sQuery(id+"F0.wireOp",EDGE,"E9"),sQuery(id+"F0.wireOp",EDGE,"E10.1.0"),sQuery(id+"F0.wireOp",EDGE,"E10.2.0")])],"isStart":true}),makeQuery(id+"F18.opExtrude","SWEPT_FACE",FACE,{"disambiguationData":[OSD([sQuery(id+"F17.wireOp",EDGE,"E53.MirrorCS")])]})]});
            var Q8;
            Q8=makeQuery(id+"F18.boolean.opBoolean","INTERSECT",EDGE,{"derivedFrom":[makeQuery(id+"F1.opExtrude","CAP_FACE",FACE,{"disambiguationData":[OSD([sQuery(id+"F0.wireOp",EDGE,"E0"),sQuery(id+"F0.wireOp",EDGE,"E2"),sQuery(id+"F0.wireOp",EDGE,"E3"),sQuery(id+"F0.wireOp",EDGE,"E4"),sQuery(id+"F0.wireOp",EDGE,"E8.1.0"),sQuery(id+"F0.wireOp",EDGE,"E8.1.4"),sQuery(id+"F0.wireOp",EDGE,"E8.1.5"),sQuery(id+"F0.wireOp",EDGE,"E8.2.0"),sQuery(id+"F0.wireOp",EDGE,"E8.2.4"),sQuery(id+"F0.wireOp",EDGE,"E8.2.5"),sQuery(id+"F0.wireOp",EDGE,"E8.3.0"),sQuery(id+"F0.wireOp",EDGE,"E8.3.4"),sQuery(id+"F0.wireOp",EDGE,"E8.3.5"),sQuery(id+"F0.wireOp",EDGE,"E8.4.0"),sQuery(id+"F0.wireOp",EDGE,"E8.4.4"),sQuery(id+"F0.wireOp",EDGE,"E8.4.5"),sQuery(id+"F0.wireOp",EDGE,"E8.5.0"),sQuery(id+"F0.wireOp",EDGE,"E8.5.4"),sQuery(id+"F0.wireOp",EDGE,"E8.5.5"),sQuery(id+"F0.wireOp",EDGE,"E9"),sQuery(id+"F0.wireOp",EDGE,"E10.1.0"),sQuery(id+"F0.wireOp",EDGE,"E10.2.0")])],"isStart":true}),makeQuery(id+"F18.opExtrude","SWEPT_FACE",FACE,{"disambiguationData":[OSD([sQuery(id+"F17.wireOp",EDGE,"E50")])]})]});
            var Q9;
            Q9=makeQuery(id+"F18.boolean.opBoolean","INTERSECT",EDGE,{"derivedFrom":[makeQuery(id+"F1.opExtrude","CAP_FACE",FACE,{"disambiguationData":[OSD([sQuery(id+"F0.wireOp",EDGE,"E0"),sQuery(id+"F0.wireOp",EDGE,"E2"),sQuery(id+"F0.wireOp",EDGE,"E3"),sQuery(id+"F0.wireOp",EDGE,"E4"),sQuery(id+"F0.wireOp",EDGE,"E8.1.0"),sQuery(id+"F0.wireOp",EDGE,"E8.1.4"),sQuery(id+"F0.wireOp",EDGE,"E8.1.5"),sQuery(id+"F0.wireOp",EDGE,"E8.2.0"),sQuery(id+"F0.wireOp",EDGE,"E8.2.4"),sQuery(id+"F0.wireOp",EDGE,"E8.2.5"),sQuery(id+"F0.wireOp",EDGE,"E8.3.0"),sQuery(id+"F0.wireOp",EDGE,"E8.3.4"),sQuery(id+"F0.wireOp",EDGE,"E8.3.5"),sQuery(id+"F0.wireOp",EDGE,"E8.4.0"),sQuery(id+"F0.wireOp",EDGE,"E8.4.4"),sQuery(id+"F0.wireOp",EDGE,"E8.4.5"),sQuery(id+"F0.wireOp",EDGE,"E8.5.0"),sQuery(id+"F0.wireOp",EDGE,"E8.5.4"),sQuery(id+"F0.wireOp",EDGE,"E8.5.5"),sQuery(id+"F0.wireOp",EDGE,"E9"),sQuery(id+"F0.wireOp",EDGE,"E10.1.0"),sQuery(id+"F0.wireOp",EDGE,"E10.2.0")])],"isStart":true}),makeQuery(id+"F18.opExtrude","SWEPT_FACE",FACE,{"disambiguationData":[OSD([sQuery(id+"F17.wireOp",EDGE,"E52")])]})]});
            var Q10;
            Q10=makeQuery(id+"F1.opExtrude","CAP_FACE",FACE,{"disambiguationData":[OSD([sQuery(id+"F0.wireOp",EDGE,"E0"),sQuery(id+"F0.wireOp",EDGE,"E2"),sQuery(id+"F0.wireOp",EDGE,"E3"),sQuery(id+"F0.wireOp",EDGE,"E4"),sQuery(id+"F0.wireOp",EDGE,"E8.1.0"),sQuery(id+"F0.wireOp",EDGE,"E8.1.4"),sQuery(id+"F0.wireOp",EDGE,"E8.1.5"),sQuery(id+"F0.wireOp",EDGE,"E8.2.0"),sQuery(id+"F0.wireOp",EDGE,"E8.2.4"),sQuery(id+"F0.wireOp",EDGE,"E8.2.5"),sQuery(id+"F0.wireOp",EDGE,"E8.3.0"),sQuery(id+"F0.wireOp",EDGE,"E8.3.4"),sQuery(id+"F0.wireOp",EDGE,"E8.3.5"),sQuery(id+"F0.wireOp",EDGE,"E8.4.0"),sQuery(id+"F0.wireOp",EDGE,"E8.4.4"),sQuery(id+"F0.wireOp",EDGE,"E8.4.5"),sQuery(id+"F0.wireOp",EDGE,"E8.5.0"),sQuery(id+"F0.wireOp",EDGE,"E8.5.4"),sQuery(id+"F0.wireOp",EDGE,"E8.5.5"),sQuery(id+"F0.wireOp",EDGE,"E9"),sQuery(id+"F0.wireOp",EDGE,"E10.1.0"),sQuery(id+"F0.wireOp",EDGE,"E10.2.0")])],"isStart":true});
            chamfer(context, id + "F19", {"entities" : qUnion([Q0, Q1, Q2, Q3, Q4, Q5, Q6, Q7, Q8, Q9, Q10]), "width" : .8 * mm, "tangentPropagation" : true});
        }
    });
